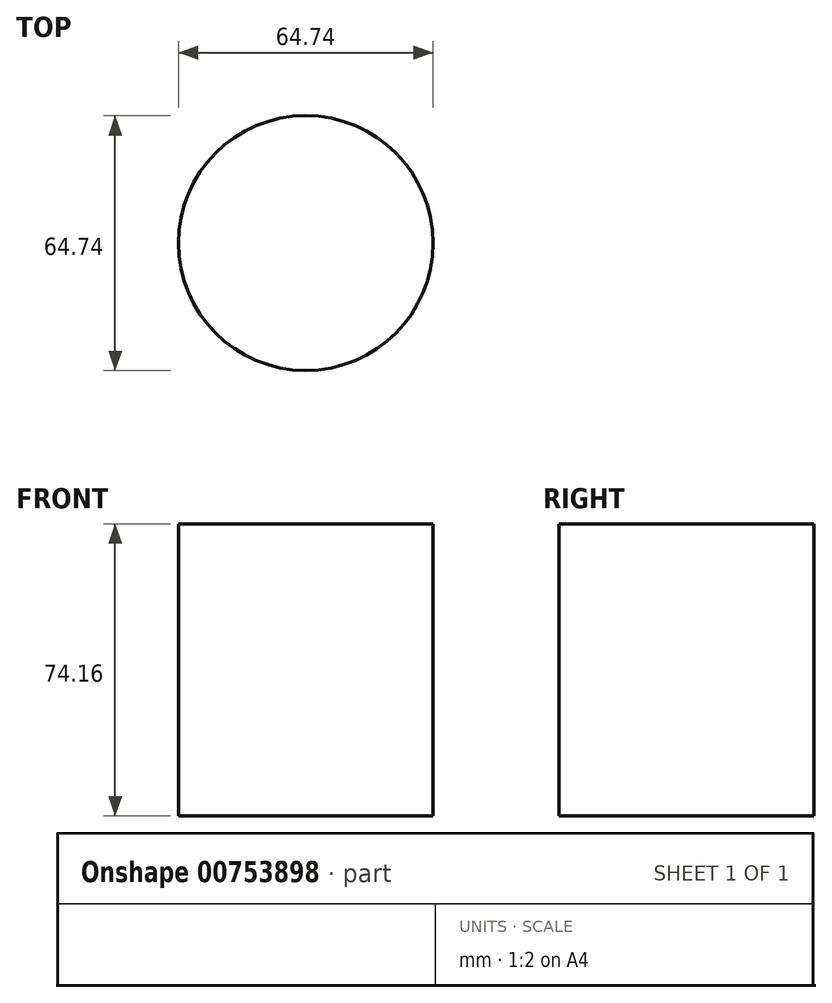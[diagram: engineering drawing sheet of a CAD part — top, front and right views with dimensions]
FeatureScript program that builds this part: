
annotation { "Feature Type Name" : "Feature", "Feature Type Description" : "" }
export const myFeature = defineFeature(function(context is Context, id is Id, definition is map)
    precondition{}
    {
        {
            var Q0;
            Q0=qCreatedBy(makeId("Top.planeOp"),FACE);
            var sketch = newSketch(context, id + "F0", { "sketchPlane" : qUnion([Q0])});
            skCircle(sketch, "E0", {"center": v(0, 0) * mm, "radius": 32.37 * mm});
            skSolve(sketch);
        }
        {
            var Q0;
            Q0 = qSketchRegion(id + "F0", true);
            extrude(context, id + "F1", {"entities" : qUnion([Q0]), "endBound" : BoundingType.SYMMETRIC, "depth" : 74.17 * mm, "offsetDistance" : 25.4 * mm});
        }
    });
